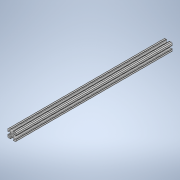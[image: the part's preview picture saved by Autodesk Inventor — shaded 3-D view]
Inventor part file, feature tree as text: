
AUTODESK INVENTOR PART (.ipt)
format: ipt  version: 2020 (Build 240168000, 168)  size: 237,056 bytes
history: native  units: in
note: dims shown in document units (in); Inventor stores cm internally (conversion verified against a paired STEP export)
features: extrude x1, sketch x1
ambient origin geometry x8: Origin, YZ Plane, XZ Plane, XY Plane, X Axis, Y Axis, Z Axis, Center Point
bodies: Solid1 (feature_tree)
feature tree (2):
  extrude  "Extrusion1"  [1 undecoded]
  sketch  "Sketch1"  dims[d0=19.0in d1=0.0in]
note: 1 required parameter value undecoded (feature->parameter linkage not recoverable at this tier; creation-order binding heuristic only, values carry confidence <= 0.55)
